# Revit family: Door_Overhead-Fold_Renlita_S-2000_Solid
name_source: partatom
category: Doors
units: mm (PartAtom-declared; Revit-internal decimal feet)

## family parameters
Always vertical = Yes
Classification Number = 23.30.10.17.37
Cut with Voids When Loaded = No
Host = Wall
Room Calculation Point = No
Shared = No

## types (2) — shared parameters
Assembly Code = B2030
Clear Opening Height = 0' - 0"
Clear Opening Width = 7' - 7"
Clearance Material = ARCAT Clearance
Description = Renlita Overhead Folding Door - S-2000 as Specified
Exterior Finish = Metal - Renlita - White
Face Thickness_Exterior = 0' - 2"
Face Thickness_Interior = 0' - 0 1/2"
Fire Rating = as Specified
Frame Finish = Metal - Renlita - White
Function = Interior
Height = 8' - 0"
Interior Finish = Metal - Renlita - White
Keynote = 8000
Manufacturer = Renlita Doors North America, LLC
Manufacturer Fax = 903-583-7544
Manufacturer Website = http://www.renlitadoors.com
Max Height = 20' - 0"
Max Width = 30' - 0"
Maximum Size = 30' W x 20' H
Model = as Specified
Opening Height = 8' - 0"
Opening Width = 8' - 0"
Panel Height = 7' - 11 1/2"
Panel Width = 7' - 11"
Product Data = http://www.arcat.com
Projection_Exterior = 2' - 11 3/4"
Projection_Interior = -2' - 9 5/8"
Rough Height = 0' - 0"
Rough Width = 0' - 0"
Sales Information = http://www.renlitadoors.com
Thickness = 0' - 0"
URL = http://www.renlitadoors.com
Wall Closure = By host
Weatherstripping Color = Finish - Black
Width = 8' - 0"
zero-valued in all types: Expected Lifespan (Years), Maintenance Schedule (Months), R-Value, Warranty Duration (Years)

## per-type parameters (varying)
| type | Motorized |
| Manual Operation | No |
| Motorized | Yes |

## geometry (parser evidence)
native form markers: Blend x8, Sweep x16
no freeform markers — native parametric forms only
